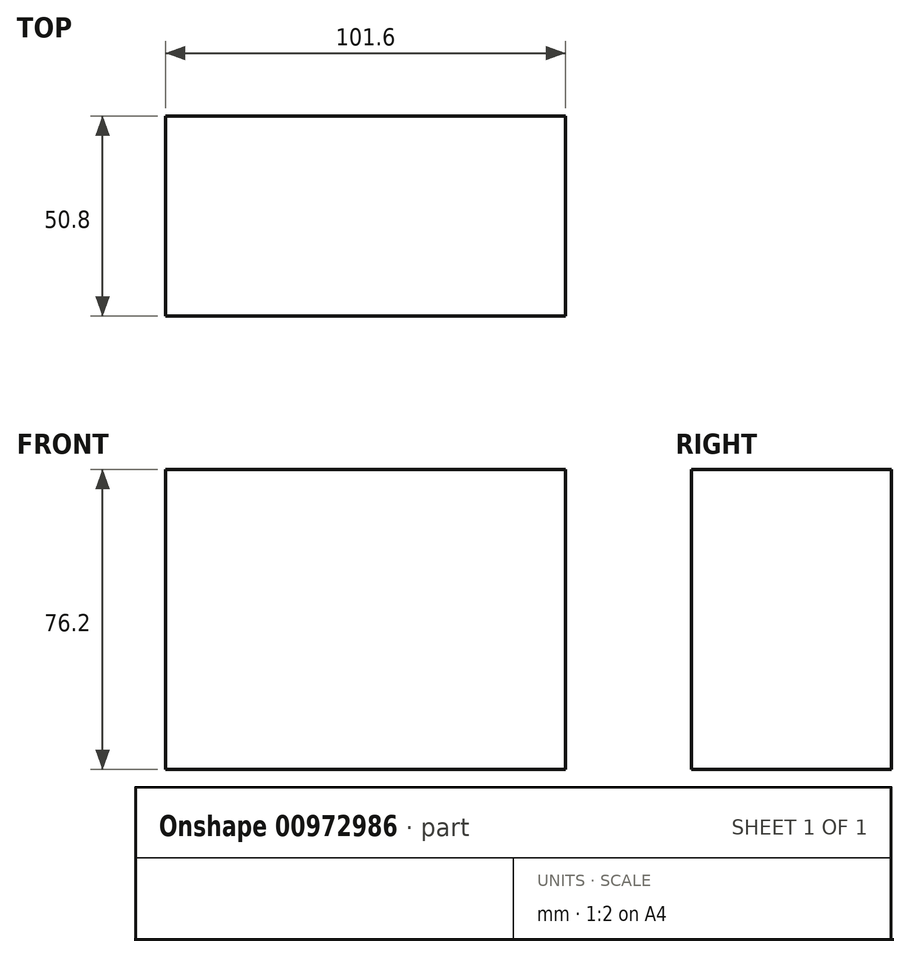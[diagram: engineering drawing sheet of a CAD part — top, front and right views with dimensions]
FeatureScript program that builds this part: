
annotation { "Feature Type Name" : "Feature", "Feature Type Description" : "" }
export const myFeature = defineFeature(function(context is Context, id is Id, definition is map)
    precondition{}
    {
        {
            var Q0;
            Q0=qCreatedBy(makeId("Front.planeOp"),FACE);
            var sketch = newSketch(context, id + "F0", { "sketchPlane" : qUnion([Q0])});
            skLineSegment(sketch, "E0.bottom", {"start": v(-50.8, 38.1) * mm, "end": v(50.8, 38.1) * mm});
            skLineSegment(sketch, "E0.top", {"start": v(-50.8, -38.1) * mm, "end": v(50.8, -38.1) * mm});
            skLineSegment(sketch, "E0.left", {"start": v(-50.8, 38.1) * mm, "end": v(-50.8, -38.1) * mm});
            skLineSegment(sketch, "E0.right", {"start": v(50.8, 38.1) * mm, "end": v(50.8, -38.1) * mm});
            skPoint(sketch, "E0.middle", {"position": v(0, 0) * mm});
            skSolve(sketch);
        }
        {
            var Q0;
            Q0=makeQuery(id+"F0.imprint","IMPRINT",FACE,{"disambiguationData":[TD([[makeQuery(id+"F0.imprint","IMPRINT",EDGE,{"derivedFrom":sQuery(id+"F0.wireOp",EDGE,"E0.bottom")}),-1.0]])]});
            var sketch = newSketch(context, id + "F1", { "sketchPlane" : qUnion([Q0])});
            skSolve(sketch);
        }
        {
            var Q0;
            Q0=makeQuery(id+"F1.imprint","IMPRINT",FACE,{"disambiguationData":[TD([[makeQuery(id+"F1.imprint","IMPRINT",EDGE,{"derivedFrom":makeQuery(id+"F0.imprint","IMPRINT",EDGE,{"derivedFrom":sQuery(id+"F0.wireOp",EDGE,"E0.bottom")})}),-1.0]])]});
            var sketch = newSketch(context, id + "F2", { "sketchPlane" : qUnion([Q0])});
            skCircle(sketch, "E1", {"center": v(0, 0) * mm, "radius": 25.4 * mm});
            skSolve(sketch);
        }
        {
            var Q0;
            Q0 = qSketchRegion(id + "F2", true);
            var Q1;
            Q1=makeQuery(id+"F1.imprint","IMPRINT",FACE,{"disambiguationData":[TD([[makeQuery(id+"F1.imprint","IMPRINT",EDGE,{"derivedFrom":makeQuery(id+"F0.imprint","IMPRINT",EDGE,{"derivedFrom":sQuery(id+"F0.wireOp",EDGE,"E0.bottom")})}),-1.0]])]});
            var Q2;
            Q2=makeQuery(id+"F0.imprint","IMPRINT",FACE,{"disambiguationData":[TD([[makeQuery(id+"F0.imprint","IMPRINT",EDGE,{"derivedFrom":sQuery(id+"F0.wireOp",EDGE,"E0.bottom")}),-1.0]])]});
            extrude(context, id + "F3", {"entities" : qUnion([Q0, Q1, Q2]), "depth" : 50.8 * mm, "offsetDistance" : 25.4 * mm});
        }
    });
